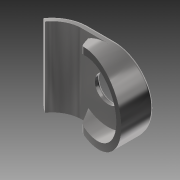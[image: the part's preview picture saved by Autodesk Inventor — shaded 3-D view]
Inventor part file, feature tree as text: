
AUTODESK INVENTOR PART (.ipt)
format: ipt  version: 2021 (Build 250183000, 183)  size: 224,768 bytes
history: native  units: mm
features: sketch x5, other x3, fillet x3, extrude x2, revolve x1, plane x1
ambient origin geometry x8: Origin, YZ Plane, XZ Plane, XY Plane, X Axis, Y Axis, Z Axis, Center Point
bodies: Body1 (feature_tree)
feature tree (15):
  other  "Sólido1"
  sketch  "Boceto1"  dims[d63=2.0mm d64=10.0mm]
  revolve  "Revolución3"  [1 undecoded]
  sketch  "Boceto5"  dims[d65=6.0mm d66=0.2mm]
  extrude  "Extrusión4"  Depth=0.2mm
  extrude  "Extrusión5"  Depth=2.0mm
  other  "Suprimir cara4"
  other  "Suprimir cara5"
  fillet  "Empalme8"  Radius=6.0mm
  fillet  "Empalme9"  Radius=8.0mm
  fillet  "Empalme10"  [1 undecoded]
  sketch  "Boceto7"  dims[d72=4.0mm]
  sketch  "Boceto8"  dims[d97=1.0mm d98=4.0mm d99=2.0mm d100=14.0mm d101=10.0mm d103=0.0mm d104=0.0mm d106=180.0deg d107=2.0mm d108=4.0mm d110=2.0mm d111=9.0mm d112=22.0mm d114=2.0mm d115=24.0mm d116=0.0mm d117=1.0mm d118=2.0mm d119=1.0mm d120=2.0mm]
  plane  "Plano de trabajo2"
  sketch  "Boceto6"  dims[d67=2.0mm d68=1.8mm d69=6.0mm d70=8.0mm d71=90.0deg]
note: 2 required parameter values undecoded (feature->parameter linkage not recoverable at this tier; creation-order binding heuristic only, values carry confidence <= 0.55)